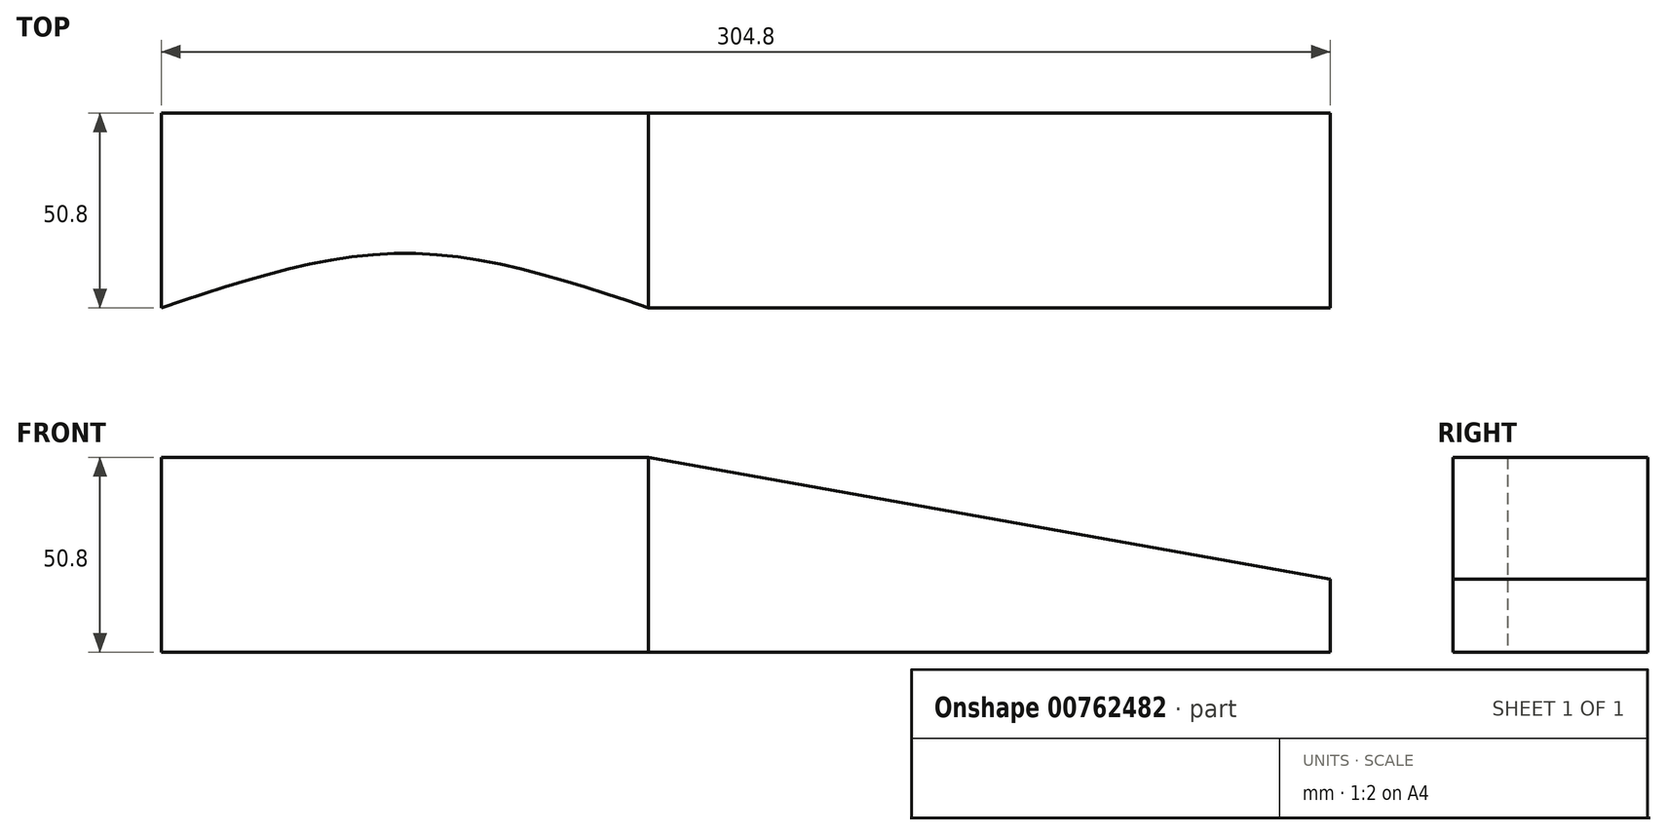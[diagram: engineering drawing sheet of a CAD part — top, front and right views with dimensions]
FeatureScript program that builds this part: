
annotation { "Feature Type Name" : "Feature", "Feature Type Description" : "" }
export const myFeature = defineFeature(function(context is Context, id is Id, definition is map)
    precondition{}
    {
        {
            var Q0;
            Q0=qCreatedBy(makeId("Front.planeOp"),FACE);
            var sketch = newSketch(context, id + "F0", { "sketchPlane" : qUnion([Q0])});
            skLineSegment(sketch, "E0", {"start": v(0, 0) * mm, "end": v(0, 50.8) * mm});
            skLineSegment(sketch, "E1", {"start": v(0, 50.8) * mm, "end": v(127, 50.8) * mm});
            skLineSegment(sketch, "E2", {"start": v(127, 50.8) * mm, "end": v(304.8, 19.05) * mm});
            skLineSegment(sketch, "E3", {"start": v(304.8, 19.05) * mm, "end": v(304.8, 0) * mm});
            skLineSegment(sketch, "E4", {"start": v(304.8, 0) * mm, "end": v(0, 0) * mm});
            skSolve(sketch);
        }
        {
            var Q0;
            Q0=makeQuery(id+"F0.imprint","IMPRINT",FACE,{"disambiguationData":[TD([[makeQuery(id+"F0.imprint","IMPRINT",EDGE,{"derivedFrom":sQuery(id+"F0.wireOp",EDGE,"E0")}),-1.0]])]});
            extrude(context, id + "F1", {"entities" : qUnion([Q0]), "oppositeDirection" : true, "depth" : 50.8 * mm, "offsetDistance" : 25.4 * mm});
        }
        {
            var Q0;
            Q0=makeQuery(id+"F1.opExtrude","SWEPT_FACE",FACE,{"disambiguationData":[OSD([sQuery(id+"F0.wireOp",EDGE,"E1")])]});
            var sketch = newSketch(context, id + "F2", { "sketchPlane" : qUnion([Q0])});
            skPoint(sketch, "E5.1.internal.snap0", {"position": v(63.5, 0) * mm});
            skFitSpline(sketch, "E5", {"points": [v(0, 0) * mm, v(63.5, 14.22) * mm, v(127, 0) * mm], "startDerivative": vector(127, 42.65) * mm, "endDerivative": vector(127, -42.65) * mm});
            skSolve(sketch);
        }
        {
            var Q0;
            Q0=makeQuery(id+"F2.imprint","IMPRINT",FACE,{"disambiguationData":[TD([[makeQuery(id+"F2.imprint","IMPRINT",EDGE,{"derivedFrom":sQuery(id+"F2.wireOp",EDGE,"E5")}),-1.0]])]});
            extrude(context, id + "F3", {"entities" : qUnion([Q0]), "operationType" : NewBodyOperationType.REMOVE, "oppositeDirection" : true, "depth" : 50.8 * mm, "offsetDistance" : 25.4 * mm});
        }
    });
